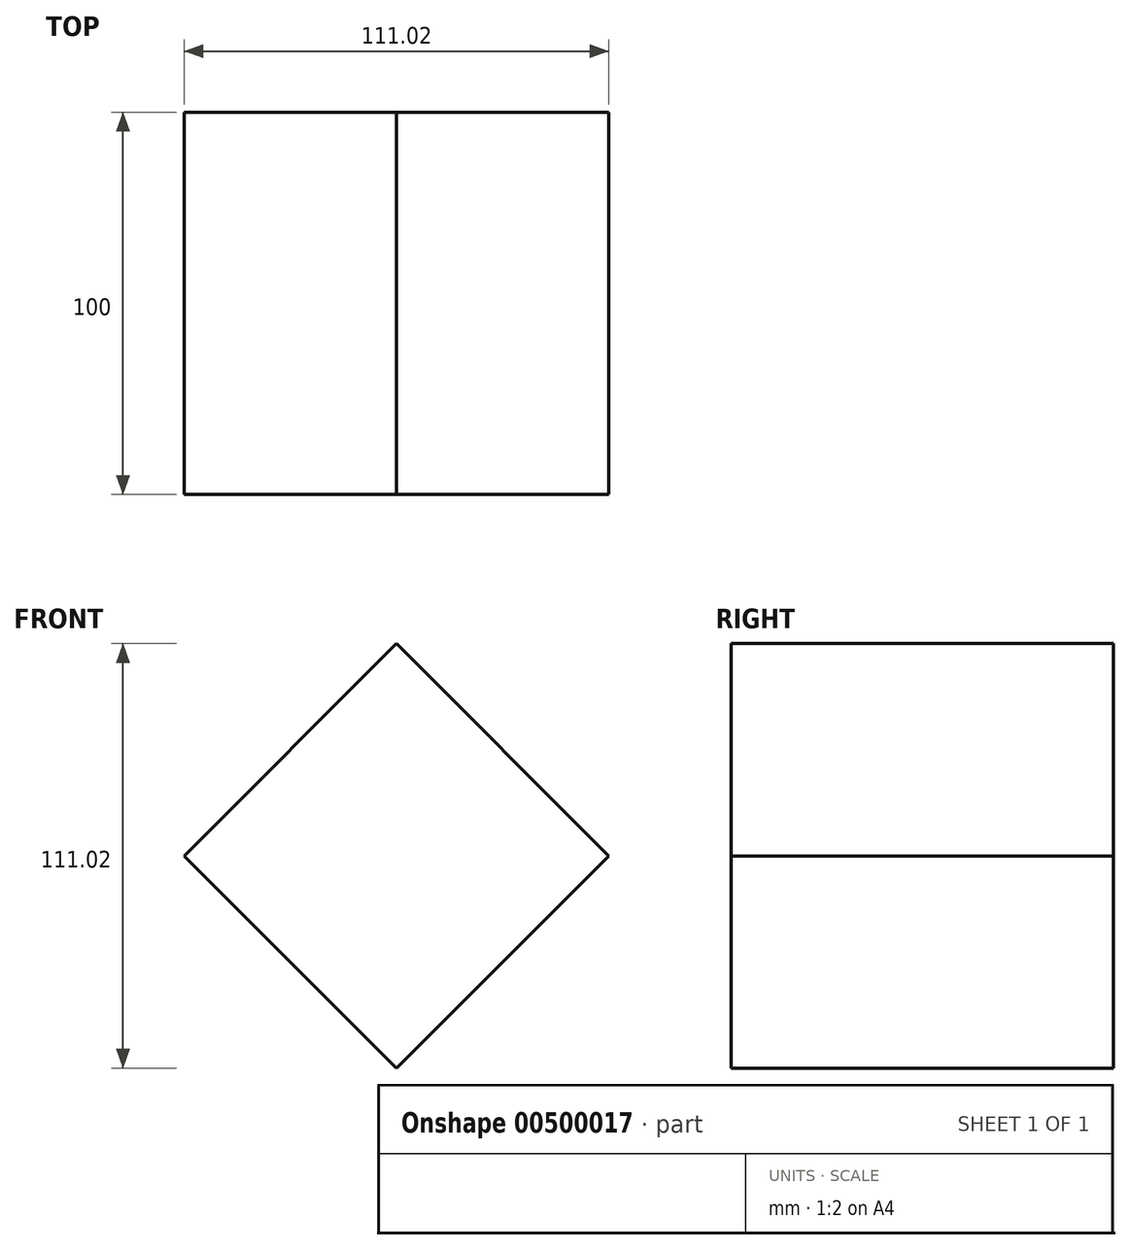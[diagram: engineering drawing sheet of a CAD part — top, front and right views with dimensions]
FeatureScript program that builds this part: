
annotation { "Feature Type Name" : "Feature", "Feature Type Description" : "" }
export const myFeature = defineFeature(function(context is Context, id is Id, definition is map)
    precondition{}
    {
        {
            var Q0;
            Q0=qCreatedBy(makeId("Front.planeOp"),FACE);
            var sketch = newSketch(context, id + "F0", { "sketchPlane" : qUnion([Q0])});
            skCircle(sketch, "E0.cCircle", {"center": v(0, 0) * mm, "radius": 55.51 * mm, "construction": true});
            skLineSegment(sketch, "E0.0", {"start": v(0, 55.51) * mm, "end": v(55.51, 0) * mm});
            skLineSegment(sketch, "E0.1", {"start": v(55.51, 0) * mm, "end": v(0, -55.51) * mm});
            skLineSegment(sketch, "E0.2", {"start": v(0, -55.51) * mm, "end": v(-55.51, 0) * mm});
            skLineSegment(sketch, "E0.3", {"start": v(-55.51, 0) * mm, "end": v(0, 55.51) * mm});
            skSolve(sketch);
        }
        {
            var Q0;
            Q0=makeQuery(id+"F0.imprint","IMPRINT",FACE,{"disambiguationData":[TD([[makeQuery(id+"F0.imprint","IMPRINT",EDGE,{"derivedFrom":sQuery(id+"F0.wireOp",EDGE,"E0.0")}),-1.0]])]});
            extrude(context, id + "F1", {"entities" : qUnion([Q0]), "endBound" : BoundingType.SYMMETRIC, "depth" : 100 * mm});
        }
    });
